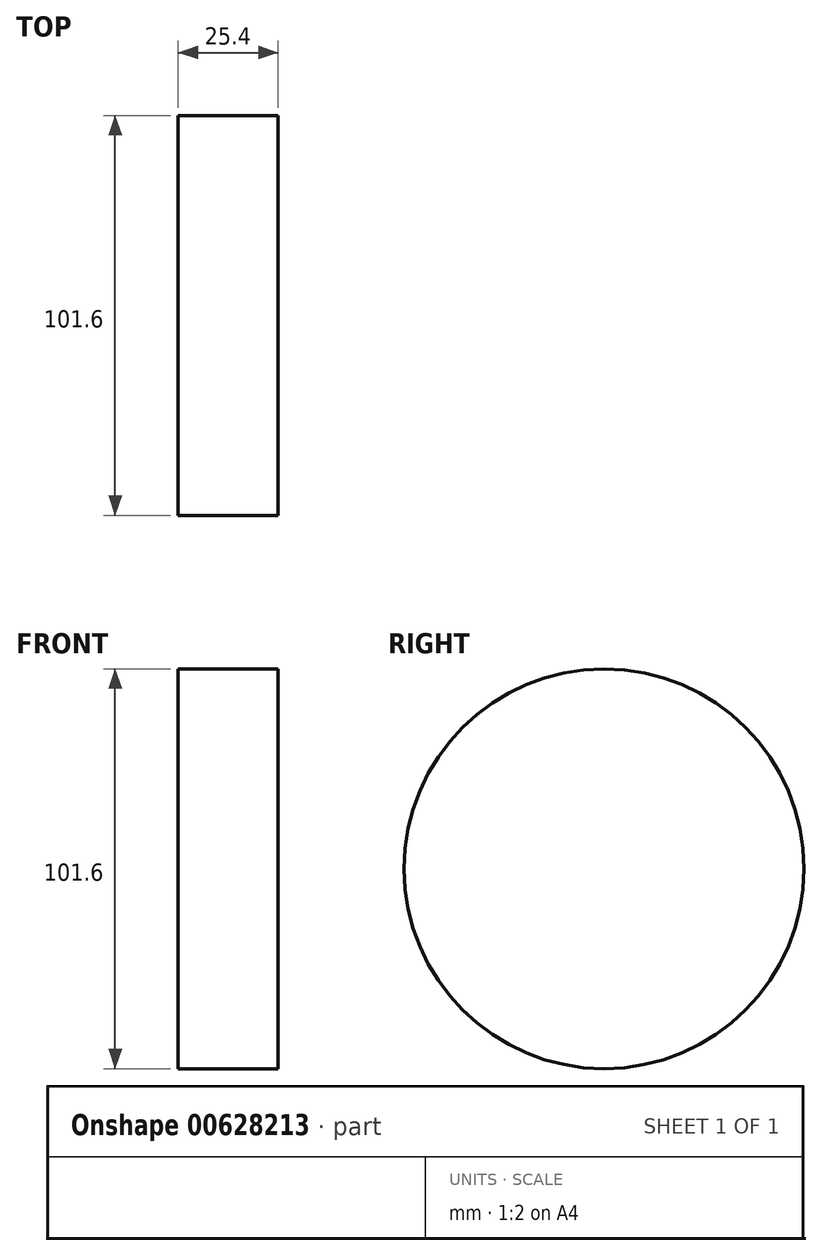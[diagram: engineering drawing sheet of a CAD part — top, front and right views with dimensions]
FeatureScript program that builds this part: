
annotation { "Feature Type Name" : "Feature", "Feature Type Description" : "" }
export const myFeature = defineFeature(function(context is Context, id is Id, definition is map)
    precondition{}
    {
        {
            var Q0;
            Q0=qCreatedBy(makeId("Front.planeOp"),FACE);
            var sketch = newSketch(context, id + "F0", { "sketchPlane" : qUnion([Q0])});
            skLineSegment(sketch, "E0.bottom", {"start": v(9.99, 19.89) * mm, "end": v(35.39, 19.89) * mm});
            skLineSegment(sketch, "E0.top", {"start": v(9.99, -30.91) * mm, "end": v(35.39, -30.91) * mm});
            skLineSegment(sketch, "E0.left", {"start": v(9.99, 19.89) * mm, "end": v(9.99, -30.91) * mm});
            skLineSegment(sketch, "E0.right", {"start": v(35.39, 19.89) * mm, "end": v(35.39, -30.91) * mm});
            skSolve(sketch);
        }
        {
            var Q0;
            Q0=makeQuery(id+"F0.imprint","IMPRINT",FACE,{"disambiguationData":[TD([[makeQuery(id+"F0.imprint","IMPRINT",EDGE,{"derivedFrom":sQuery(id+"F0.wireOp",EDGE,"E0.bottom")}),-1.0]])]});
            var Q1;
            Q1=sQuery(id+"F0.wireOp",EDGE,"E0.bottom");
            revolve(context, id + "F1", {"entities" : qUnion([Q0]), "axis" : qUnion([Q1]), "revolveType" : RevolveType.FULL});
        }
    });
